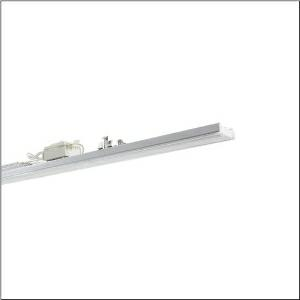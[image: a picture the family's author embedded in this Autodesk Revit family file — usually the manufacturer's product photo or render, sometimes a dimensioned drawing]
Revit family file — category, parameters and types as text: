
# Revit family: licross_r__21_recessed_mo_52tl12dn48xg_e767
name_source: partatom
category: Lighting Fixtures
units: mm (PartAtom-declared; Revit-internal decimal feet)

## family parameters
Cut with Voids When Loaded = No
Host = Face
Light Source = No
Part Type = Normal
Room Calculation Point = No
Round Connector Dimension = Use Diameter
Shared = No

## types (1)
- --- (1 x LED, 8000 lm, 44.2 W, 4000K)
    Apparent Load = 44 VA
    CIE Flux Codes = 72 92 99 100 100
    Color Rendering = 80
    Color Temperature = 4000K
    Default Elevation = 1800 mm
    Description = Licross® 21 Recessed MO, luminaire insert, of sheet steel, galvanised, coil coated, white, length: 1.500mm, width: 66mm, height: 67mm, LED rated luminous flux: 8.000lm, light colour: 840, control gear: DALI 2, with plug, 5-pole, with phase selection, mains connection: 220..240V, AC, 50/60Hz, rated input power: 44W, halogen-free wiring, primary optical cover: cover, of PMMA, light emission: direct distribution, primary light characteristic: symmetric, protection rating (complete): IP40, insulation class (complete): insulation class I (protective earthing), certification: CE, ENEC, VDE, UKCA, protection symbol: D if used in an environment without relevant dust loads with corresponding accessories, impact resistance: IK06, permissible ambient temperature for indoor applications: -25..+40°C, corresponds to IFS (International Featured Standards) requirements for safety and quality in the food industry, reducing of maximum allowable ambient temperature of 5°C with ceiling mounting, LABS conformity tested according to VDMA 24364:2018-05, packaging unit: 1 piece
    Height = 58 mm
    Lamp = 1 x LED
    Lamp Light Flux = 8000 lm
    Lamp Power = 44.2 W
    Lamp count = 1
    Length = 1500 mm
    Luminous efficacy = 181 lm/W
    Manufacturer = Siteco
    ModVariant = No
    Model = 52TL12DN48XG
    Mounting Place = Ceiling
    Mounting Type = Pendant
    Number of Poles = 1
    OnlyDefault = Yes
    Power Factor = 1
    Product Name = Licross® 21 Recessed MO
    Product group = luminaire insert
    ProductGroupID = 902
    Protection Class = Protection class I
    Protection Degree = IP 40
    RLX_Detail_Level = 1
    RLX_Emergency_Light_Flux = 0 lm
    RLX_Emergency_Type = 0
    RLX_Emergency_Type_DB = No
    RlxData = <blob elided: 24597 chars, md5=1d7c720c>
    Socket = socket
    Standby Power = 0 W
    System Light Flux = 8000 lm
    System Power = 44 W
    Type Comments = factory setting: luminous flux: 100 % | dim-lin: 254 | 297 mA
    Type Image = l_1296930.jpg
    URL = http://relux.com
    VarID = @adj_126174
    Voltage = 0 V
    Weight = 0.00 kg
    Width = 66 mm

## geometry (parser evidence)
native form markers: Blend x4, Sweep x11
no freeform markers — native parametric forms only
